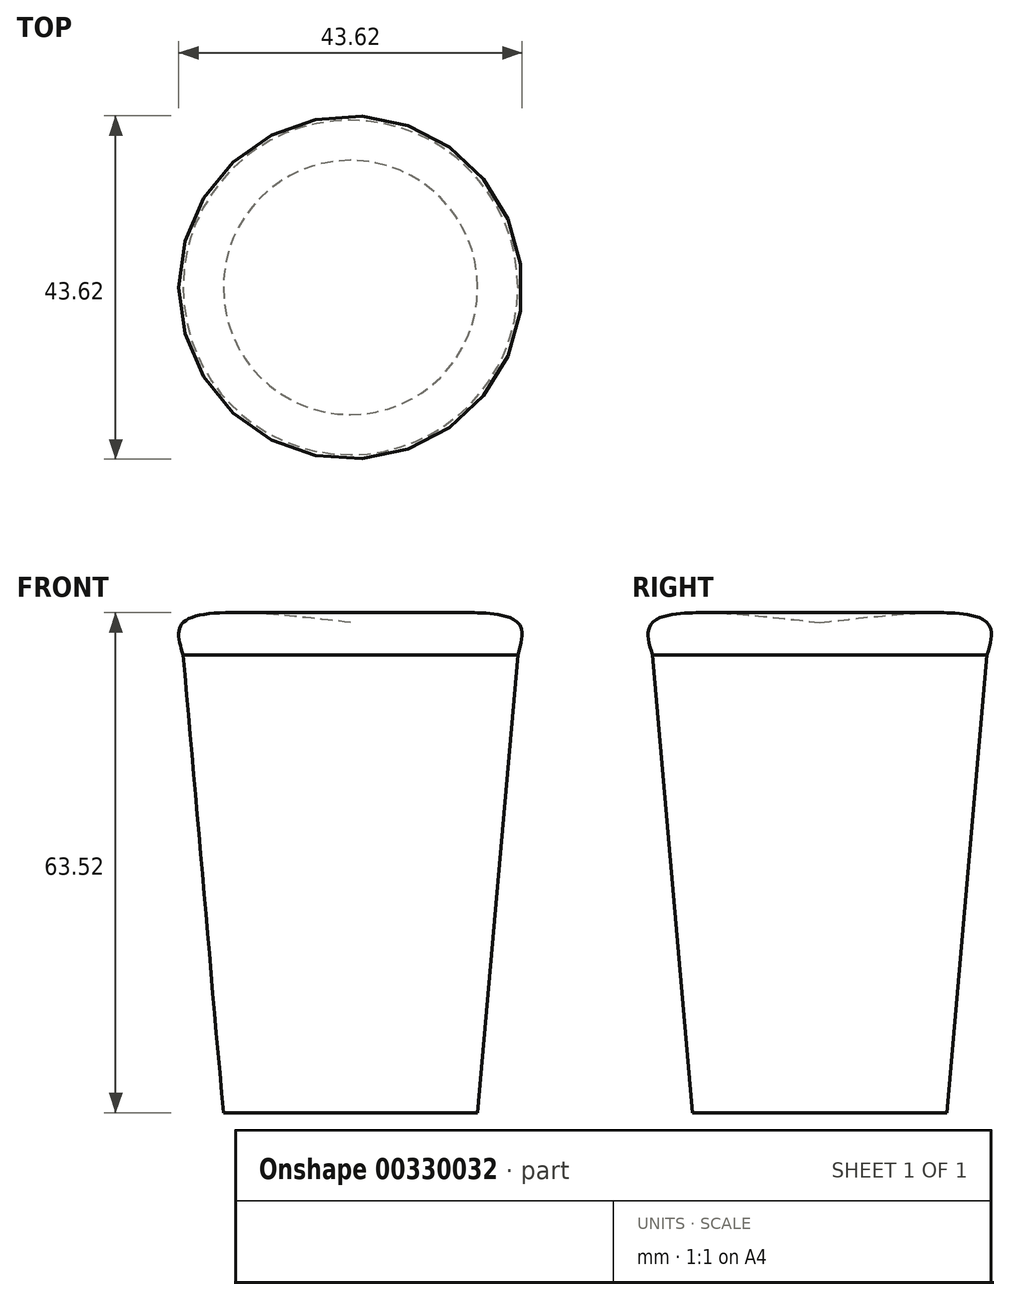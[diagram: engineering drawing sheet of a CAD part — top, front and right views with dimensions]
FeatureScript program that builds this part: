
annotation { "Feature Type Name" : "Feature", "Feature Type Description" : "" }
export const myFeature = defineFeature(function(context is Context, id is Id, definition is map)
    precondition{}
    {
        {
            var Q0;
            Q0=qCreatedBy(makeId("Front.planeOp"),FACE);
            var sketch = newSketch(context, id + "F0", { "sketchPlane" : qUnion([Q0])});
            skFitSpline(sketch, "E0", {"points": [v(0, 45.4) * mm, v(-21.25, 45.4) * mm, v(-21.25, 41.27) * mm], "startDerivative": vector(-41.26, 4.69) * mm, "endDerivative": vector(4.69, -15.58) * mm});
            skLineSegment(sketch, "E1", {"start": v(-21.25, 41.27) * mm, "end": v(0, 41.27) * mm});
            skLineSegment(sketch, "E2", {"start": v(-21.25, 41.27) * mm, "end": v(-16.15, -16.86) * mm});
            skLineSegment(sketch, "E3", {"start": v(-16.15, -16.86) * mm, "end": v(0, -16.86) * mm});
            skLineSegment(sketch, "E4", {"start": v(0, -16.86) * mm, "end": v(0, 41.27) * mm});
            skLineSegment(sketch, "E5", {"start": v(0, 45.4) * mm, "end": v(0, 41.27) * mm});
            skSolve(sketch);
        }
        {
            var Q0;
            Q0=makeQuery(id+"F0.imprint","IMPRINT",FACE,{"disambiguationData":[TD([[makeQuery(id+"F0.imprint","IMPRINT",EDGE,{"derivedFrom":sQuery(id+"F0.wireOp",EDGE,"E1")}),-1.0]])]});
            var Q1;
            Q1=makeQuery(id+"F0.imprint","IMPRINT",FACE,{"disambiguationData":[TD([[makeQuery(id+"F0.imprint","IMPRINT",EDGE,{"derivedFrom":sQuery(id+"F0.wireOp",EDGE,"E0")}),1.0]])]});
            var Q2;
            Q2=sQuery(id+"F0.wireOp",EDGE,"E4");
            revolve(context, id + "F1", {"entities" : qUnion([Q0, Q1]), "axis" : qUnion([Q2]), "revolveType" : RevolveType.FULL});
        }
        {
            var Q0;
            Q0=makeQuery(id+"F1.opRevolve","SWEPT_FACE",FACE,{"disambiguationData":[OSD([sQuery(id+"F0.wireOp",EDGE,"E3")])]});
            cPlane(context, id + "F2", {"entities" : qUnion([Q0]), "cplaneType" : CPlaneType.OFFSET, "offset" : 60.45 * mm, "oppositeDirection" : true, "width" : 152.4 * mm, "height" : 152.4 * mm});
        }
    });
